# Revit family: Plumbing Fixture_GalvinSpecialised_Floor_Drain_SS_69468X_F
name_source: partatom
category: Plumbing Fixtures
units: mm (PartAtom-declared; Revit-internal decimal feet)

## family parameters
Cut with Voids When Loaded = No
Host = Face
Part Type = Normal
Room Calculation Point = No
Round Connector Dimension = Use Diameter
Shared = No

## types (1)
- Type 1
    Anti_Ligature = No
    Application = Commercial
    CW Connection = No
    CategoryStyleOrType_ANZRS = Plumbing Fixture
    Default Elevation = 1219 mm
    Description = SS Slip-Safe Vinyl Bolted Cleanout 150 x 100 PVC/HDPE/CU Slip-In
    HW Connection = No
    Manufacturer = Galvin Engineering
    Manufacturer_OverallDepth = 0 mm  [stored 0 ft]
    Manufacturer_OverallHeight = 0 mm  [stored 0 ft]
    Manufacturer_OverallWidth = 0 mm  [stored 0 ft]
    Mounting = Floor
    Mounting_Surface = Floor
    PlumbingFinish = SS/ABS
    PlumbingMaterial_ANZRS = SS
    Product_Range = Specialised
    Product_Type = Drain
    SKU_Code = 69468X
    Specify_Host = Face
    URL = http://www.galvinengineering.com.au
    Vandal_Resistant = No
    Vent Connection = No
    Waste Connection = No

note: [stored X ft] marks values corroborated as IEEE doubles in the binary element streams (Revit-internal decimal feet)

## geometry (parser evidence)
native form markers: Sweep x14
no freeform markers — native parametric forms only
